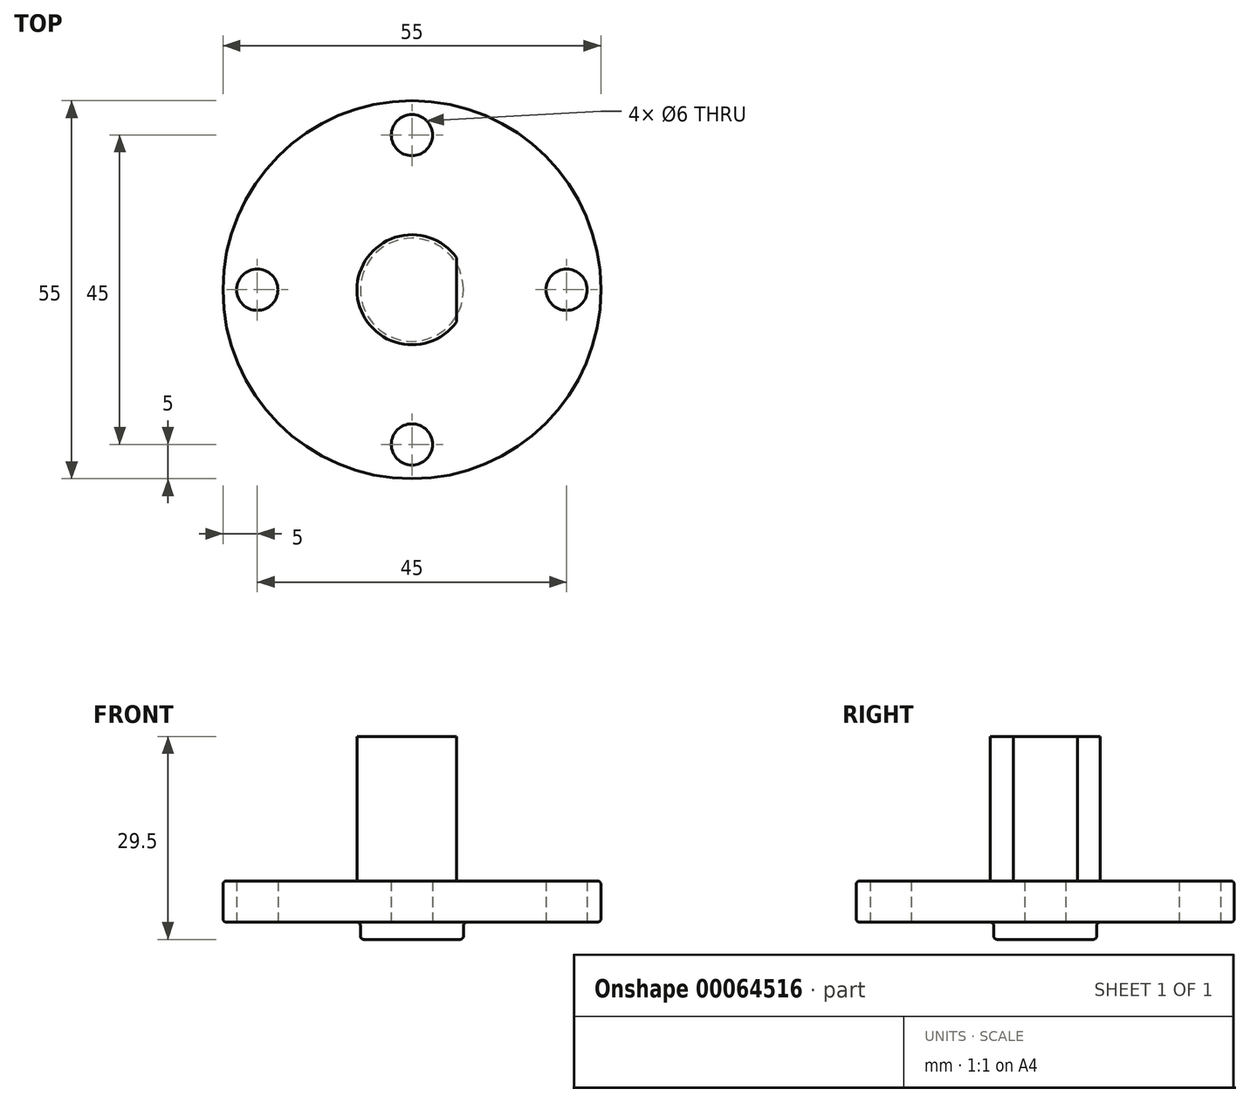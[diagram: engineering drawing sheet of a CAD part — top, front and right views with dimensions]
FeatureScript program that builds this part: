
annotation { "Feature Type Name" : "Feature", "Feature Type Description" : "" }
export const myFeature = defineFeature(function(context is Context, id is Id, definition is map)
    precondition{}
    {
        {
            var Q0;
            Q0=qCreatedBy(makeId("Front.planeOp"),FACE);
            var sketch = newSketch(context, id + "F0", { "sketchPlane" : qUnion([Q0])});
            skLineSegment(sketch, "E0", {"start": v(0, -2.5) * mm, "end": v(-7.5, -2.5) * mm});
            skLineSegment(sketch, "E1", {"start": v(-7.5, -2.5) * mm, "end": v(-7.5, 0) * mm});
            skLineSegment(sketch, "E2", {"start": v(-7.5, 0) * mm, "end": v(-27.5, 0) * mm});
            skLineSegment(sketch, "E3", {"start": v(-27.5, 0) * mm, "end": v(-27.5, 6) * mm});
            skLineSegment(sketch, "E4", {"start": v(-27.5, 6) * mm, "end": v(-8, 6) * mm});
            skLineSegment(sketch, "E5", {"start": v(-8, 6) * mm, "end": v(-8, 27) * mm});
            skLineSegment(sketch, "E6", {"start": v(-8, 27) * mm, "end": v(0, 27) * mm});
            skLineSegment(sketch, "E7", {"start": v(0, 27) * mm, "end": v(0, -2.5) * mm});
            skLineSegment(sketch, "E8", {"start": v(0, 23.73) * mm, "end": v(0, -12.53) * mm, "construction": true});
            skSolve(sketch);
        }
        {
            var Q0;
            Q0 = qSketchRegion(id + "F0", true);
            var Q1;
            Q1=sQuery(id+"F0.wireOp",EDGE,"E8");
            revolve(context, id + "F1", {"entities" : qUnion([Q0]), "axis" : qUnion([Q1]), "revolveType" : RevolveType.FULL});
        }
        {
            var Q0;
            Q0=qCreatedBy(makeId("Top.planeOp"),FACE);
            var sketch = newSketch(context, id + "F2", { "sketchPlane" : qUnion([Q0])});
            skCircle(sketch, "E9", {"center": v(0, 0) * mm, "radius": 22.5 * mm, "construction": true});
            skLineSegment(sketch, "E10", {"start": v(-36.93, 0) * mm, "end": v(44.65, 0) * mm, "construction": true});
            skLineSegment(sketch, "E11", {"start": v(0, -42.44) * mm, "end": v(0, 40.02) * mm, "construction": true});
            skPoint(sketch, "E12", {"position": v(0, -22.5) * mm});
            skPoint(sketch, "E13", {"position": v(-22.5, 0) * mm});
            skPoint(sketch, "E14", {"position": v(22.5, 0) * mm});
            skPoint(sketch, "E15", {"position": v(0, 22.5) * mm});
            skSolve(sketch);
        }
        {
            var Q0;
            Q0=sQuery(id+"F2.wireOp",VERTEX,"E12");
            var Q1;
            Q1=sQuery(id+"F2.wireOp",VERTEX,"E14");
            var Q2;
            Q2=sQuery(id+"F2.wireOp",VERTEX,"E15");
            var Q3;
            Q3=sQuery(id+"F2.wireOp",VERTEX,"E13");
            var Q4;
            Q4=makeQuery(id+"F1.opRevolve","SWEPT_BODY",BODY,{"disambiguationData":[OSD([sQuery(id+"F0.wireOp",EDGE,"E0"),sQuery(id+"F0.wireOp",EDGE,"E1"),sQuery(id+"F0.wireOp",EDGE,"E2"),sQuery(id+"F0.wireOp",EDGE,"E3"),sQuery(id+"F0.wireOp",EDGE,"E4"),sQuery(id+"F0.wireOp",EDGE,"E5"),sQuery(id+"F0.wireOp",EDGE,"E6"),sQuery(id+"F0.wireOp",EDGE,"E7")])]});
            hole(context, id + "F3", {"style" : HoleStyle.SIMPLE, "holeDiameter" : 6 * mm, "endStyle" : HoleEndStyle.THROUGH, "oppositeDirection" : true, "locations" : qUnion([Q0, Q1, Q2, Q3]), "scope" : qUnion([Q4])});
        }
        {
            var Q0;
            Q0=makeQuery(id+"F1.opRevolve","SWEPT_EDGE",EDGE,{"disambiguationData":[OSD([sQuery(id+"F0.wireOp",EDGE,"E3"),sQuery(id+"F0.wireOp",EDGE,"E4")])]});
            var Q1;
            Q1=makeQuery(id+"F1.opRevolve","SWEPT_EDGE",EDGE,{"disambiguationData":[OSD([sQuery(id+"F0.wireOp",EDGE,"E2"),sQuery(id+"F0.wireOp",EDGE,"E3")])]});
            var Q2;
            Q2=makeQuery(id+"F1.opRevolve","SWEPT_EDGE",EDGE,{"disambiguationData":[OSD([sQuery(id+"F0.wireOp",EDGE,"E0"),sQuery(id+"F0.wireOp",EDGE,"E1")])]});
            var Q3;
            Q3=makeQuery(id+"F1.opRevolve","SWEPT_EDGE",EDGE,{"disambiguationData":[OSD([sQuery(id+"F0.wireOp",EDGE,"E1"),sQuery(id+"F0.wireOp",EDGE,"E2")])]});
            fillet(context, id + "F4", {"entities" : qUnion([Q0, Q1, Q2, Q3]), "radius" : .5 * mm, "tangentPropagation" : true, "allowEdgeOverflow" : false});
        }
        {
            var Q0;
            Q0=qCreatedBy(makeId("Right.planeOp"),FACE);
            cPlane(context, id + "F5", {"entities" : qUnion([Q0]), "cplaneType" : CPlaneType.OFFSET, "offset" : 6.5 * mm, "width" : 150 * mm, "height" : 150 * mm});
        }
        {
            var Q0;
            Q0=qCreatedBy(id+"F5.planeOp",FACE);
            var sketch = newSketch(context, id + "F6", { "sketchPlane" : qUnion([Q0])});
            skLineSegment(sketch, "E16", {"start": v(-4.66, 6) * mm, "end": v(-4.66, 27) * mm});
            skLineSegment(sketch, "E17", {"start": v(4.66, 27) * mm, "end": v(4.66, 6) * mm});
            skLineSegment(sketch, "E18", {"start": v(-4.66, 6) * mm, "end": v(4.66, 6) * mm});
            skLineSegment(sketch, "E19", {"start": v(-4.66, 27) * mm, "end": v(4.66, 27) * mm});
            skSolve(sketch);
        }
        {
            var Q0;
            Q0 = qSketchRegion(id + "F6", true);
            extrude(context, id + "F7", {"entities" : qUnion([Q0]), "operationType" : NewBodyOperationType.REMOVE, "depth" : 25 * mm});
        }
    });
